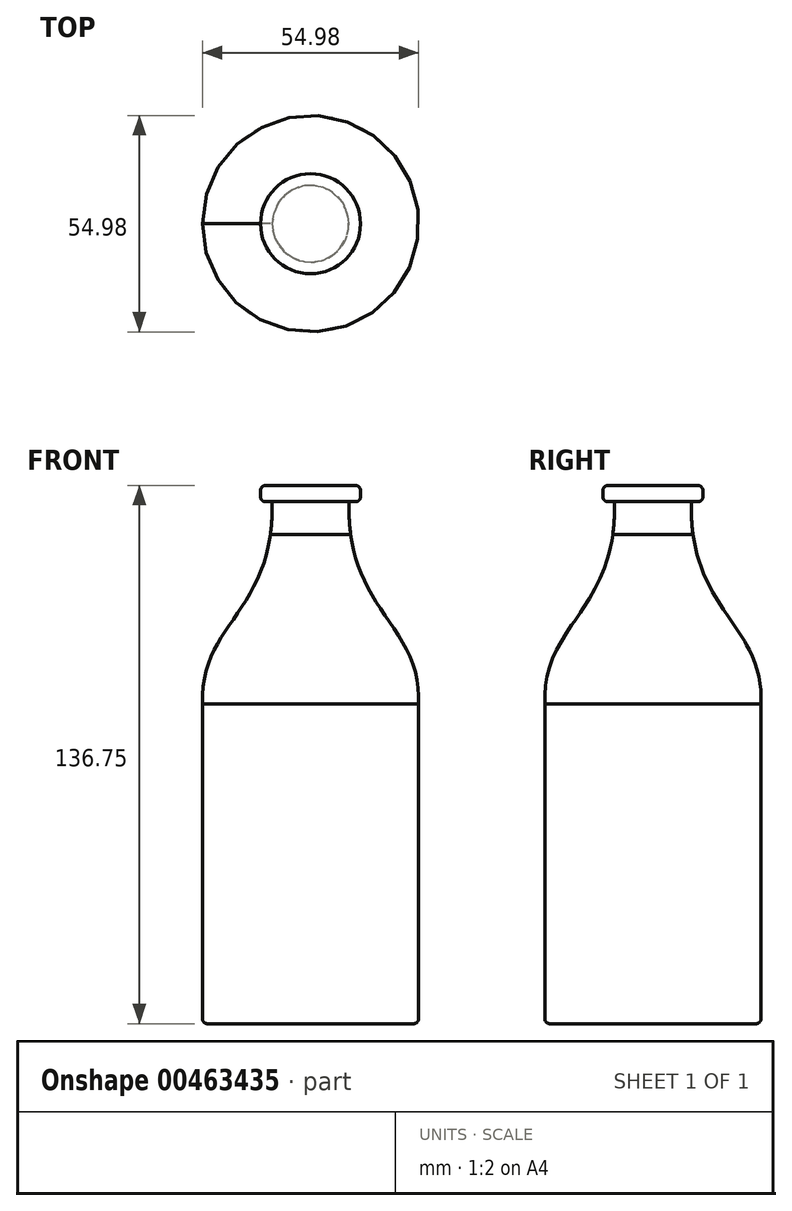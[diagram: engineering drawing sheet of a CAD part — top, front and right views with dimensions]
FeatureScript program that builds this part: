
annotation { "Feature Type Name" : "Feature", "Feature Type Description" : "" }
export const myFeature = defineFeature(function(context is Context, id is Id, definition is map)
    precondition{}
    {
        {
            var Q0;
            Q0=qCreatedBy(makeId("Front.planeOp"),FACE);
            var sketch = newSketch(context, id + "F0", { "sketchPlane" : qUnion([Q0])});
            skLineSegment(sketch, "E0.bottom", {"start": v(0, -41.2) * mm, "end": v(-27.47, -41.2) * mm});
            skLineSegment(sketch, "E0.top", {"start": v(0, 40.02) * mm, "end": v(-27.47, 40.02) * mm});
            skLineSegment(sketch, "E0.left", {"start": v(0, -41.2) * mm, "end": v(0, 40.02) * mm});
            skLineSegment(sketch, "E0.right", {"start": v(-27.47, -41.2) * mm, "end": v(-27.47, 40.02) * mm});
            skLineSegment(sketch, "E1", {"start": v(0, 40.02) * mm, "end": v(0, 91.41) * mm});
            skLineSegment(sketch, "E2", {"start": v(0, 91.41) * mm, "end": v(-9.75, 91.41) * mm});
            skFitSpline(sketch, "E3", {"points": [v(-9.75, 91.41) * mm, v(-27.47, 40.02) * mm], "startDerivative": vector(1.77, -84.17) * mm, "endDerivative": vector(2.27, -61.78) * mm});
            skLineSegment(sketch, "E4", {"start": v(0, 83.14) * mm, "end": v(-10.2, 83.14) * mm});
            skLineSegment(sketch, "E5", {"start": v(0, 91.41) * mm, "end": v(0, 95.55) * mm});
            skLineSegment(sketch, "E6", {"start": v(0, 95.55) * mm, "end": v(-12.7, 95.55) * mm});
            skLineSegment(sketch, "E7", {"start": v(-12.7, 95.55) * mm, "end": v(-12.7, 91.41) * mm});
            skLineSegment(sketch, "E8", {"start": v(-12.7, 91.41) * mm, "end": v(-9.75, 91.41) * mm});
            skSolve(sketch);
        }
        {
            var Q0;
            Q0=makeQuery(id+"F0.imprint","IMPRINT",FACE,{"disambiguationData":[TD([[makeQuery(id+"F0.imprint","IMPRINT",EDGE,{"derivedFrom":sQuery(id+"F0.wireOp",EDGE,"E0.bottom")}),-1.0]])]});
            var Q1;
            Q1=sQuery(id+"F0.wireOp",EDGE,"E0.left");
            revolve(context, id + "F1", {"entities" : qUnion([Q0]), "axis" : qUnion([Q1]), "revolveType" : RevolveType.FULL});
        }
        {
            var Q0;
            {var subQ0=sQuery(id+"F0.wireOp",EDGE,"E0.top");Q0=makeQuery(id+"F0.imprint","IMPRINT",FACE,{"disambiguationData":[TD([[makeQuery(id+"F0.imprint","IMPRINT",EDGE,{"derivedFrom":subQ0}),-1.0]])]});}
            var Q1;
            Q1=sQuery(id+"F0.wireOp",EDGE,"E1");
            revolve(context, id + "F2", {"operationType" : NewBodyOperationType.ADD, "entities" : qUnion([Q0]), "axis" : qUnion([Q1]), "revolveType" : RevolveType.FULL});
        }
        {
            var Q0;
            {var subQ0=sQuery(id+"F0.wireOp",EDGE,"E2");Q0=makeQuery(id+"F0.imprint","IMPRINT",FACE,{"disambiguationData":[TD([[makeQuery(id+"F0.imprint","IMPRINT",EDGE,{"derivedFrom":subQ0}),1.0]])]});}
            var Q1;
            Q1=sQuery(id+"F0.wireOp",EDGE,"E1");
            revolve(context, id + "F3", {"operationType" : NewBodyOperationType.ADD, "entities" : qUnion([Q0]), "axis" : qUnion([Q1]), "revolveType" : RevolveType.FULL});
        }
        {
            var Q0;
            Q0=makeQuery(id+"F0.imprint","IMPRINT",FACE,{"disambiguationData":[TD([[makeQuery(id+"F0.imprint","IMPRINT",EDGE,{"derivedFrom":sQuery(id+"F0.wireOp",EDGE,"E2")}),-1.0]])]});
            var Q1;
            Q1=sQuery(id+"F0.wireOp",EDGE,"E5");
            revolve(context, id + "F4", {"operationType" : NewBodyOperationType.ADD, "entities" : qUnion([Q0]), "axis" : qUnion([Q1]), "revolveType" : RevolveType.FULL});
        }
        {
            var Q0;
            Q0=makeQuery(id+"F4.opRevolve","SWEPT_EDGE",EDGE,{"disambiguationData":[OSD([sQuery(id+"F0.wireOp",EDGE,"E7"),sQuery(id+"F0.wireOp",EDGE,"E8")])]});
            var Q1;
            Q1=makeQuery(id+"F4.opRevolve","SWEPT_EDGE",EDGE,{"disambiguationData":[OSD([sQuery(id+"F0.wireOp",EDGE,"E6"),sQuery(id+"F0.wireOp",EDGE,"E7")])]});
            var Q2;
            Q2=makeQuery(id+"F1.opRevolve","SWEPT_EDGE",EDGE,{"disambiguationData":[OSD([sQuery(id+"F0.wireOp",EDGE,"E0.bottom"),sQuery(id+"F0.wireOp",EDGE,"E0.right")])]});
            fillet(context, id + "F5", {"entities" : qUnion([Q0, Q1, Q2]), "radius" : 1.27 * mm, "tangentPropagation" : true, "allowEdgeOverflow" : false});
        }
    });
